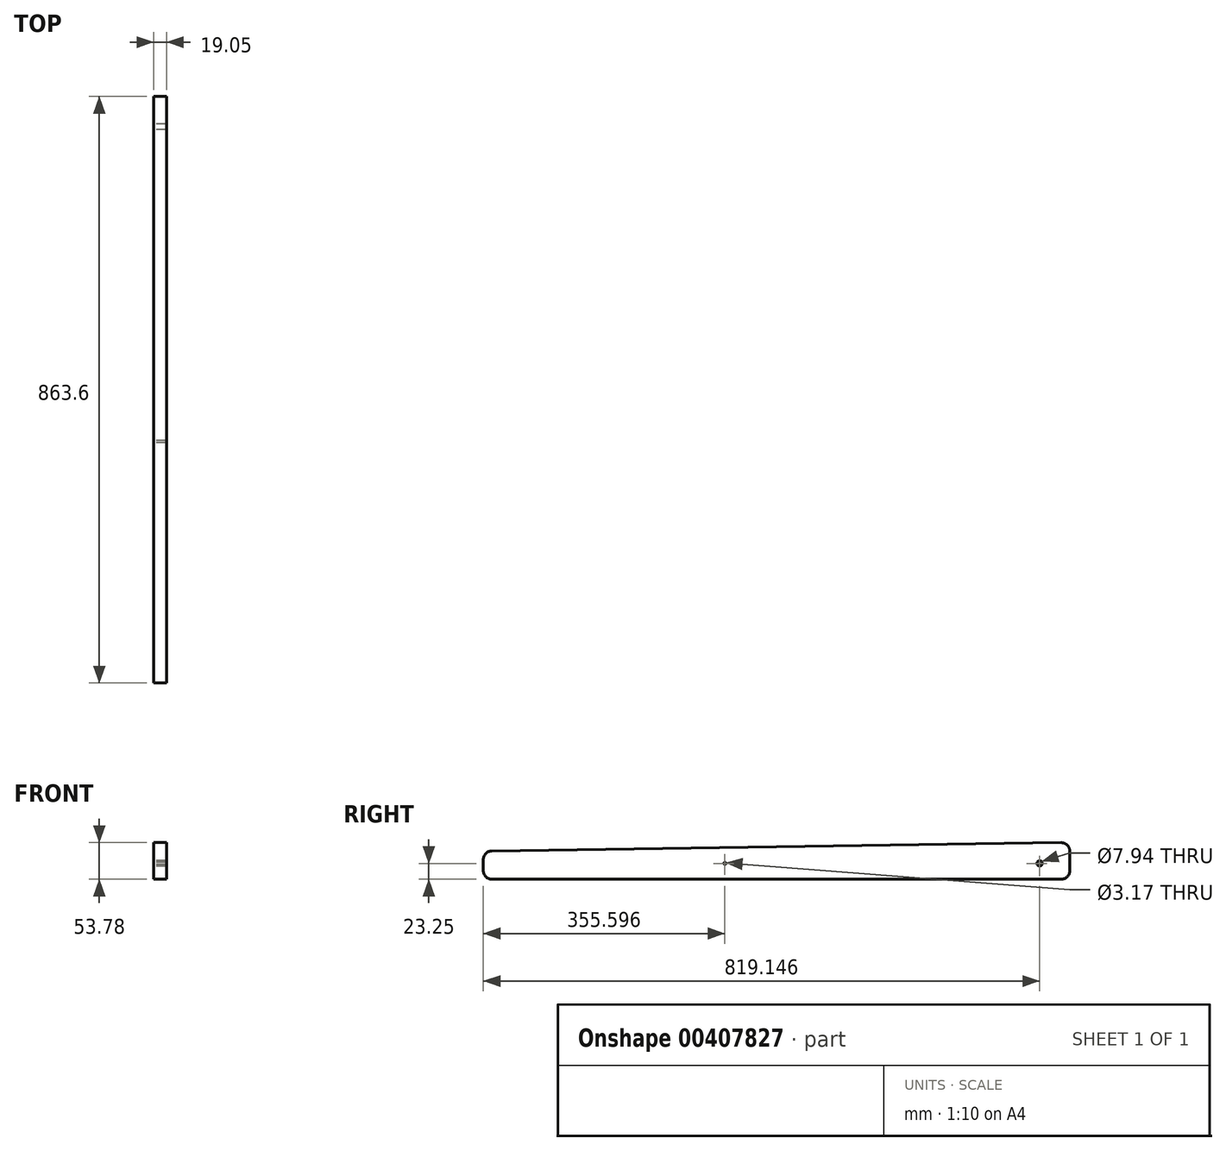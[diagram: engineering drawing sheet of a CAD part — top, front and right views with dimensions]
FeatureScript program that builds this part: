
annotation { "Feature Type Name" : "Feature", "Feature Type Description" : "" }
export const myFeature = defineFeature(function(context is Context, id is Id, definition is map)
    precondition{}
    {
        {
            var Q0;
            Q0=qCreatedBy(makeId("Right.planeOp"),FACE);
            var sketch = newSketch(context, id + "F0", { "sketchPlane" : qUnion([Q0])});
            skLineSegment(sketch, "E0", {"start": v(414.53, 17.83) * mm, "end": v(414.53, -10.55) * mm});
            skLineSegment(sketch, "E1", {"start": v(401.83, -23.25) * mm, "end": v(-436.37, -23.25) * mm});
            skLineSegment(sketch, "E2", {"start": v(-449.07, -10.55) * mm, "end": v(-449.07, 5.5) * mm});
            skLineSegment(sketch, "E3", {"start": v(-436.56, 18.2) * mm, "end": v(401.64, 30.53) * mm});
            skCircle(sketch, "E4", {"center": v(370.08, 0) * mm, "radius": 3.97 * mm});
            skCircle(sketch, "E5", {"center": v(-93.47, 0) * mm, "radius": 1.59 * mm});
            skPoint(sketch, "E6", {"position": v(-93.47, 23.25) * mm});
            skPoint(sketch, "E7", {"position": v(-93.47, -23.25) * mm});
            skPoint(sketch, "E8.visualSharp", {"position": v(414.53, 30.72) * mm});
            skArc(sketch, "E8.filletArc", {"start": v(414.53, 17.83) * mm, "mid": v(410.74, 26.88) * mm, "end": v(401.64, 30.53) * mm});
            skPoint(sketch, "E9.visualSharp", {"position": v(414.53, -23.25) * mm});
            skArc(sketch, "E9.filletArc", {"start": v(401.83, -23.25) * mm, "mid": v(410.8, -19.53) * mm, "end": v(414.53, -10.55) * mm});
            skPoint(sketch, "E10.visualSharp", {"position": v(-449.07, 18.02) * mm});
            skArc(sketch, "E10.filletArc", {"start": v(-436.56, 18.2) * mm, "mid": v(-445.42, 14.42) * mm, "end": v(-449.07, 5.5) * mm});
            skPoint(sketch, "E11.visualSharp", {"position": v(-449.07, -23.25) * mm});
            skArc(sketch, "E11.filletArc", {"start": v(-449.07, -10.55) * mm, "mid": v(-445.35, -19.53) * mm, "end": v(-436.37, -23.25) * mm});
            skSolve(sketch);
        }
        {
            var Q0;
            Q0=makeQuery(id+"F0.imprint","IMPRINT",FACE,{"disambiguationData":[TD([[makeQuery(id+"F0.imprint","IMPRINT",EDGE,{"derivedFrom":sQuery(id+"F0.wireOp",EDGE,"E0")}),-1.0]])]});
            extrude(context, id + "F1", {"entities" : qUnion([Q0]), "depth" : 19.05 * mm});
        }
        {
            var Q0;
            Q0=makeQuery(id+"F1.opExtrude","SWEPT_FACE",FACE,{"disambiguationData":[OSD([sQuery(id+"F0.wireOp",EDGE,"E1")])]});
            var sketch = newSketch(context, id + "F2", { "sketchPlane" : qUnion([Q0])});
            skCircle(sketch, "E12", {"center": v(9.53, -668.53) * mm, "radius": 1.59 * mm});
            skSolve(sketch);
        }
        {
            var Q0;
            Q0=makeQuery(id+"F2.imprint","IMPRINT",FACE,{"disambiguationData":[TD([[makeQuery(id+"F2.imprint","IMPRINT",EDGE,{"derivedFrom":sQuery(id+"F2.wireOp",EDGE,"E12")}),1.0]])]});
            extrude(context, id + "F3", {"entities" : qUnion([Q0]), "operationType" : NewBodyOperationType.REMOVE, "oppositeDirection" : true, "depth" : 52.58 * mm});
        }
    });
